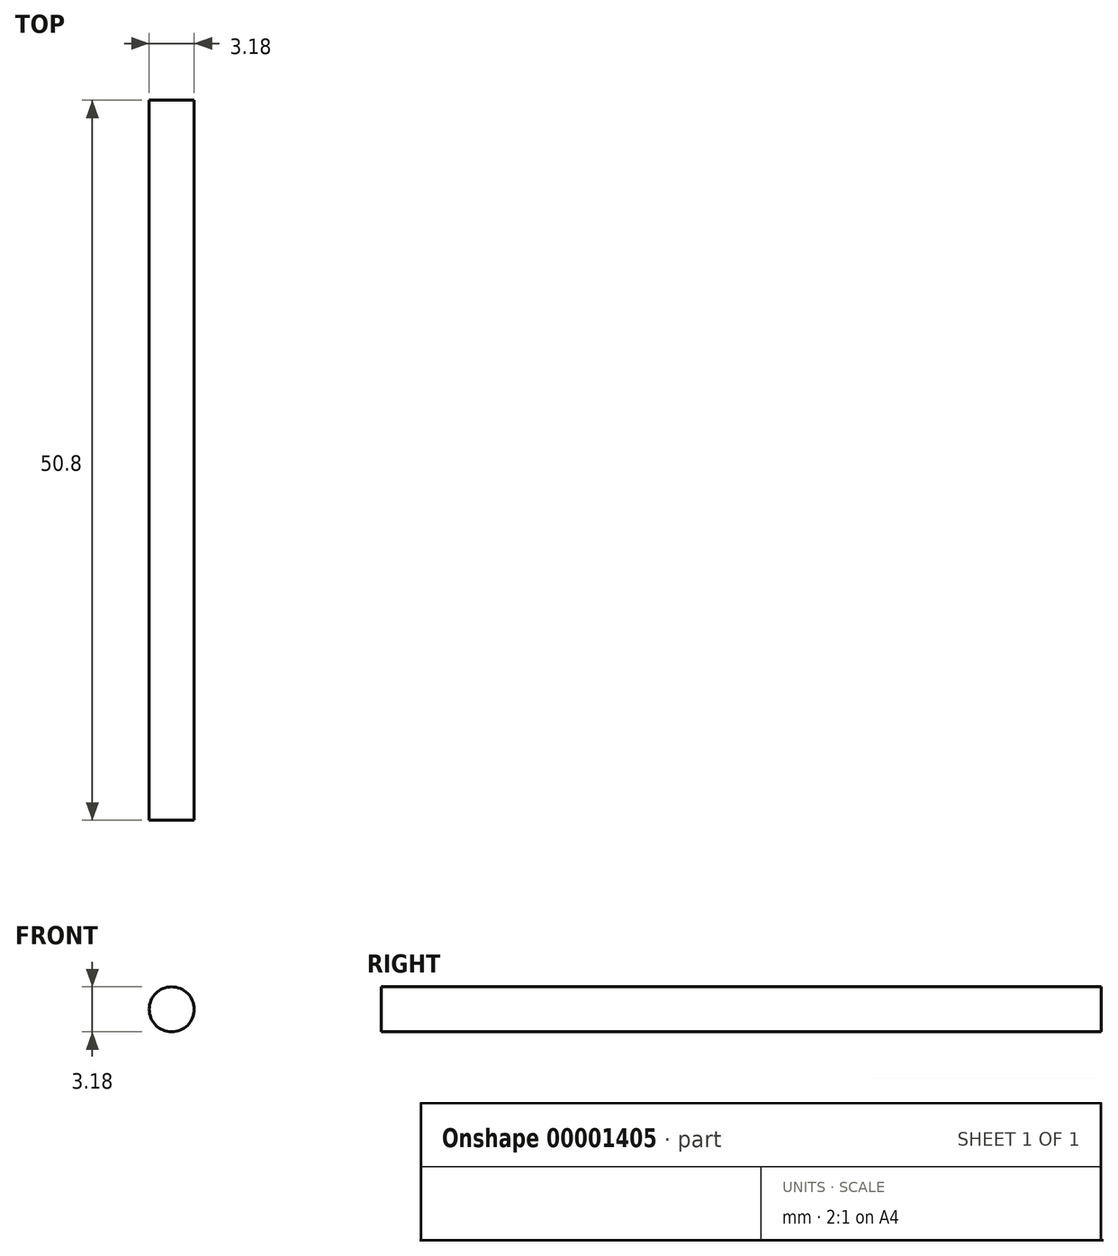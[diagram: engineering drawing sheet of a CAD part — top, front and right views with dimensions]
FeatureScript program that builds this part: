
annotation { "Feature Type Name" : "Feature", "Feature Type Description" : "" }
export const myFeature = defineFeature(function(context is Context, id is Id, definition is map)
    precondition{}
    {
        {
            var Q0;
            Q0=qCreatedBy(makeId("Front.planeOp"),FACE);
            var sketch = newSketch(context, id + "F0", { "sketchPlane" : qUnion([Q0])});
            skCircle(sketch, "E0", {"center": v(0, 0) * mm, "radius": 1.59 * mm});
            skSolve(sketch);
        }
        {
            var Q0;
            Q0 = qSketchRegion(id + "F0", true);
            extrude(context, id + "F1", {"entities" : qUnion([Q0]), "endBound" : BoundingType.SYMMETRIC, "depth" : 50.8 * mm});
        }
    });
